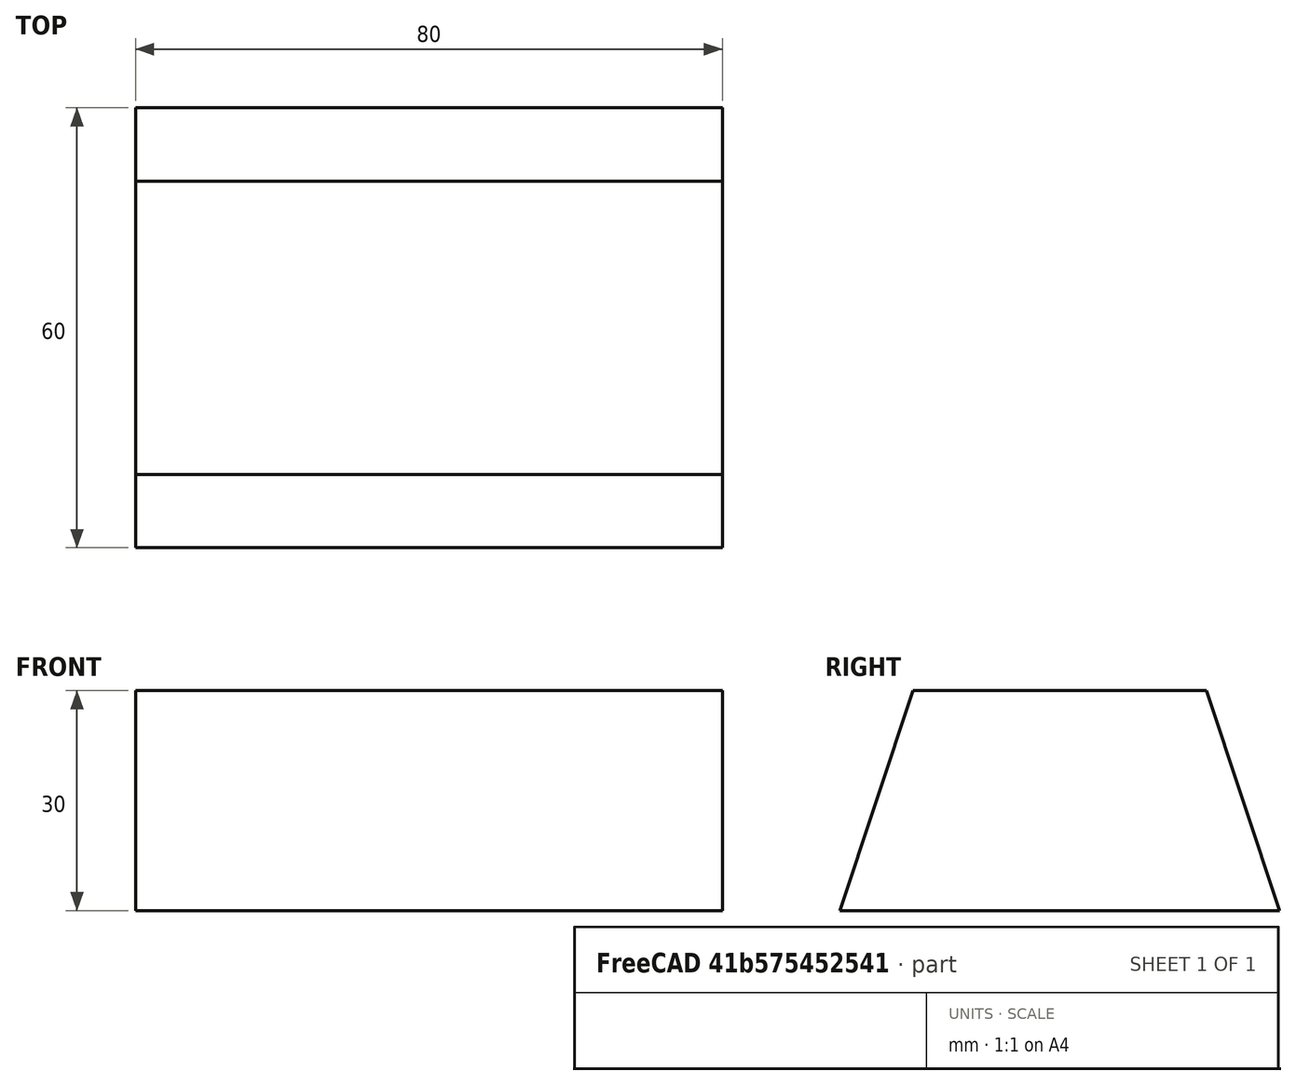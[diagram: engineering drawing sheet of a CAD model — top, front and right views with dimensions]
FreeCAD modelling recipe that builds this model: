
FCSTD DOCUMENT  (FreeCAD 0.18.4R)
Label: tutorial_freecad_ex16_b
License: All rights reserved
LicenseURL: http://en.wikipedia.org/wiki/All_rights_reserved
objects: Sketcher::SketchObject×1, PartDesign::Pad×1, PartDesign::Body×1
note: 4 computed .brp shape members not serialized (recipe doc carries the construction recipe); baked Part::Feature solids carry a one-line shape summary decoded from their .brp

FEATURE [Sketcher::SketchObject] Sketch  label="boceto_lingote"
  MapMode = 5
  Placement = pos=(0,0,0) rot=(0.57735,0.57735,0.57735;2.0944rad)
  Support = -> [YZ_Plane]
  sketch-geometry (4):
    g0: LineSegment StartX=-30 StartY=0 StartZ=0 EndX=30 EndY=0 EndZ=0
    g1: LineSegment StartX=30 StartY=0 StartZ=0 EndX=20 EndY=30 EndZ=0
    g2: LineSegment StartX=20 StartY=30 StartZ=0 EndX=-20 EndY=30 EndZ=0
    g3: LineSegment StartX=-20 StartY=30 StartZ=0 EndX=-30 EndY=0 EndZ=0
  constraints (4):
    c: Coincident(g0,g1)
    c: Coincident(g1,g2)
    c: Coincident(g2,g3)
    c: Coincident(g3,g0)
FEATURE [PartDesign::Pad] Pad  label="lingote_pad"
  Length = 80
  Length2 = 100
  Placement = pos=(0,0,0) rot=(0.57735,0.57735,0.57735;2.0944rad)
  Profile = -> Sketch
  Refine = true
  Type = 0
FEATURE [PartDesign::Body] Body  label="lingote"
  Group = -> [Sketch,Pad]
  Origin = -> Origin
  Tip = -> Pad
